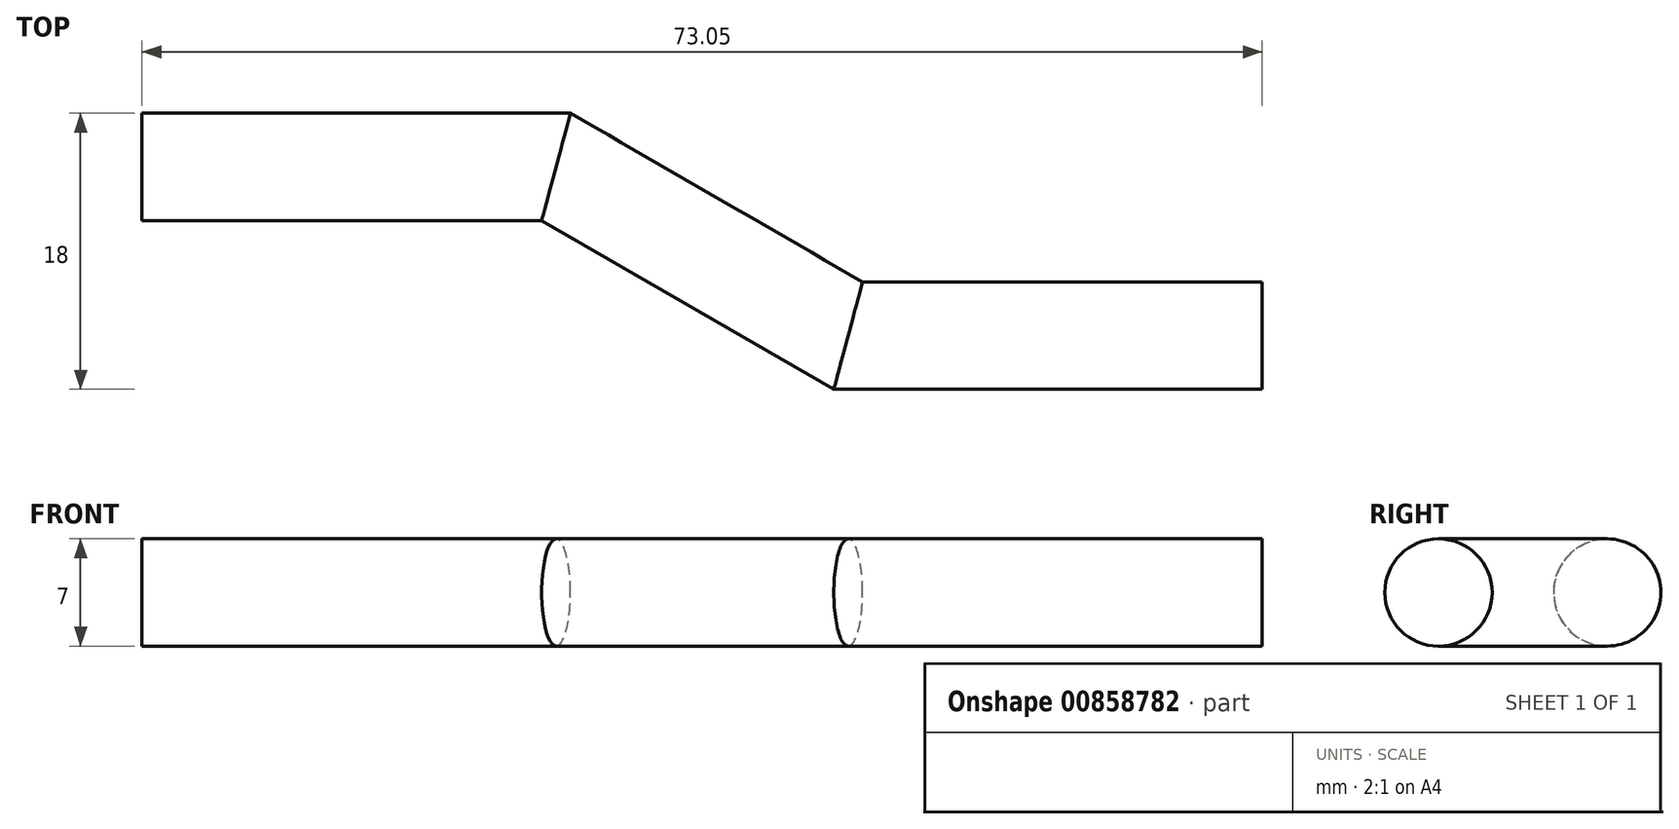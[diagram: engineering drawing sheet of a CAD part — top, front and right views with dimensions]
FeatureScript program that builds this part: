
annotation { "Feature Type Name" : "Feature", "Feature Type Description" : "" }
export const myFeature = defineFeature(function(context is Context, id is Id, definition is map)
    precondition{}
    {
        {
            var Q0;
            Q0=qCreatedBy(makeId("Top.planeOp"),FACE);
            var sketch = newSketch(context, id + "F0", { "sketchPlane" : qUnion([Q0])});
            skLineSegment(sketch, "E0", {"start": v(0, 0) * mm, "end": v(27, 0) * mm});
            skLineSegment(sketch, "E1", {"start": v(27, 0) * mm, "end": v(46.05, -11) * mm});
            skLineSegment(sketch, "E2", {"start": v(46.05, -11) * mm, "end": v(73.05, -11) * mm});
            skSolve(sketch);
        }
        {
            var Q0;
            Q0=qCreatedBy(makeId("Right.planeOp"),FACE);
            var sketch = newSketch(context, id + "F1", { "sketchPlane" : qUnion([Q0])});
            skCircle(sketch, "E3", {"center": v(0, 0) * mm, "radius": 3.5 * mm});
            skSolve(sketch);
        }
        {
            var Q0;
            Q0=makeQuery(id+"F1.imprint","IMPRINT",FACE,{"disambiguationData":[TD([[makeQuery(id+"F1.imprint","IMPRINT",EDGE,{"derivedFrom":sQuery(id+"F1.wireOp",EDGE,"E3")}),1.0]])]});
            var Q1;
            Q1 = qSketchRegion(id + "F0", true);
            var Q2;
            Q2=sQuery(id+"F0.wireOp",EDGE,"E0");
            var Q3;
            Q3=sQuery(id+"F0.wireOp",EDGE,"E1");
            var Q4;
            Q4=sQuery(id+"F0.wireOp",EDGE,"E2");
            sweep(context, id + "F2", {"profiles" : qUnion([Q0, Q1]), "path" : qUnion([Q2, Q3, Q4])});
        }
    });
